# Revit family: 05-7983-05-F9
name_source: partatom
category: Luminarias
revit_build: Autodesk Revit 2017 (Build: 20160225_1515(x64)
units: mm (PartAtom-declared; Revit-internal decimal feet)

## family parameters
Compartido = Sí
Corte con vacíos al cargar = No
Cota de conector redondo = Diámetro de uso
Número OmniClass = 23.80.70.00
Origen de luz = No
Punto de cálculo de habitación = No
Se basa en plano de trabajo = No
Siempre vertical = Sí
Tipo de pieza = Normal
Título OmniClass = Lighting

## types (1)
- 05-7983-05-F9
    Acabado = Negro, Arenado
    CRI = 90
    Catálogo = Decorative
    CodigoGubimclass = 50.60.50.20
    CodigoOmniclass = 21-04 50 40
    CodigoUniclass2015 = EF_70_80
    CodigoUniformat2010 = D5040
    DescripcionGubimclass = Iluminación interior
    DescripcionOmniclass = Lighting
    DescripcionUniclass2015 = Lighting
    DescripcionUniformat2010 = Lighting
    EAN13 = 8435575321755
    Eficiencia energética = LED A++
    Etiqueta V/f = 100-240V/50-60Hz
    Fabricante = LEDS C4
    Familia = Dresde Led
    FechaVersion = Julio 2020
    Ficha = http://files.leds-c4.com
    Fotometría = http://files.leds-c4.com
    IMC = http://files.leds-c4.com
    IP = IP44
    IfcExportAs = IfcLightFixture
    IfcExportType = NOTDEFINED
    Imagen web = http://files.leds-c4.com
    LDT = http://files.leds-c4.com
    Lumenes reales (lm) = 563
    Material = Aluminio, Cristal
    Peso neto (KG) = 0.54
    Producto descatalogado = Catalogado ES
    Referencia = 05-7983-05-F9
    Temperatura color led (K) = Blanco cálido - 3000K
    Tender text (Castellano) = LEDS C4
Dresde Led
05-7983-05-F9

Aplique de uso interior para iluminar hacia arriba. 
Material estructura: Aluminio. Acabado estructura: Negro. Material difusor: Cristal. Acabado difusor: Arenado. Garantía: 5 Años.

Peso neto del producto (Kg): 0.540
Anchura o diámetro del producto (mm): 55
Altura del producto (mm): 267
Salida del producto (mm): 90

Clase 2. IP: IP44. LED. Nº de portalámparas o Leds: 1. Marca del LED: CREE. Marca del Driver: HEP. Potencia máxima de la fuente de luz: 7.5W. Temperatura de color: Blanco cálido - 3000K. Índice de reproducción cromática: 90. Steps Mac Adam: 3. Diámetro máximo de la bombilla que admite la luminaria: 50.000h L80B20. UGR:  9.4. Riesgo fotobiológico: RG2. Flujo real (lm): 563. Lm/W reales: 59. Rango de voltaje/frecuencia: 90-264/50-60Hz. Voltaje: 18. Equipo incluido: Si, electrónico. Potencia total: 9.5. Factor de potencia: 0.90.
    Tender text (English) = LEDS C4
Dresde Led
05-7983-05-F9

Wall light for indoor use. 

For uplighting.. Structure material: Aluminium. Structure finish: Black. Diffuser material: Glass. Diffuser finish: Sandblasted. Warranty: 5 Years.

Product net weight (Kg): 0.540
Product width or diameter (mm): 55
Product height (mm): 267
Product aperture (mm): 90

Class 2. IP: IP44. LED. No. of lampholders or LEDs: 1. LED brand: CREE. Driver brand: HEP. Maximum power of light source: 7.5W. Colour temperature: LED warm-white 3000K. Colour rendering index: 90. MacAdam Steps: 3. Maximum diameter of luminaire bulb: 50.000h L80B20. UGR:  9.4. Photobiological risk: RG2. Real flux (lm): 563. Lm/Real W: 59. Voltage and frequency range: 90-264/50-60Hz. Voltage: 18. Gear included: Yes, electronic. Total power: 9.5. Power factor: 0.90.
    Tipo = Baño
    Vatios (W) = 9.5
    Versión = v1
